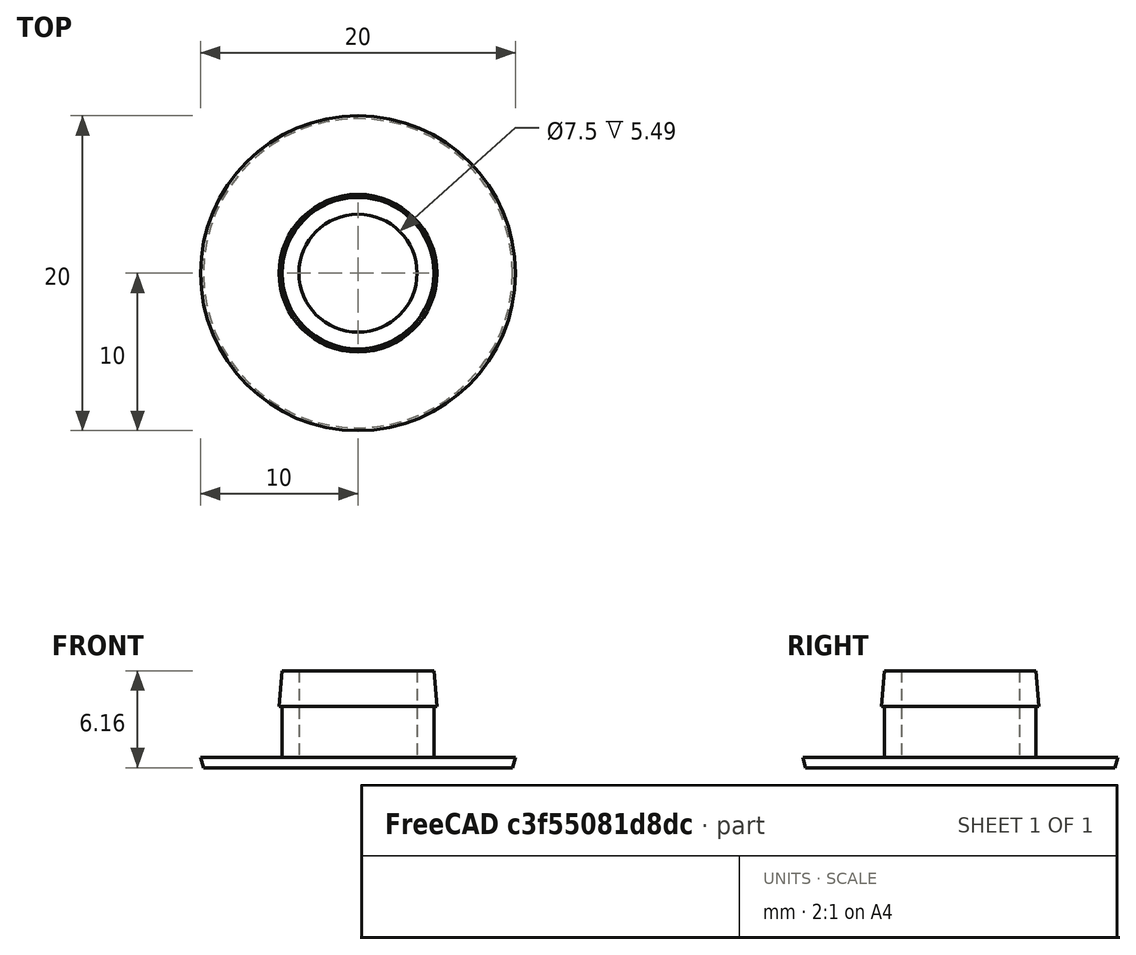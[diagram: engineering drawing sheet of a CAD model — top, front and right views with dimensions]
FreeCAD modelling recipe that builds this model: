
FCSTD DOCUMENT  (FreeCAD 0.20R29177 +426 (Git))
Label: door_threshold_screw_cover_9_3mm
License: Creative Commons Attribution
LicenseURL: http://creativecommons.org/licenses/by/3.0/
objects: Sketcher::SketchObject×1, PartDesign::Revolution×1, PartDesign::Body×1, Mesh::Feature×1
note: 4 computed .brp shape members not serialized (recipe doc carries the construction recipe); baked Part::Feature solids carry a one-line shape summary decoded from their .brp

FEATURE [Sketcher::SketchObject] Sketch
  FullyConstrained = true
  MapMode = 5
  Placement = pos=(0,0,0) rot=(1,0,0;1.5708rad)
  Support = -> [XZ_Plane]
  expr: .Constraints.Inner = 9.640000000000001 / 2
  expr: .Constraints.Outer = 20 / 2
  expr: Constraints[10] = .Constraints.Inner
  expr: Constraints[19] = .Constraints.Thickness
  expr: Constraints[20] = 7.5 / 2
  expr: Constraints[26] = .Constraints.Inner
  sketch-geometry (11):
    g0: LineSegment StartX=0 StartY=0 StartZ=0 EndX=-4.82 EndY=0 EndZ=0
    g1: LineSegment StartX=-10 StartY=0.67 StartZ=0 EndX=-4.82 EndY=0.67 EndZ=0
    g2: LineSegment StartX=-4.82 StartY=0.67 StartZ=0 EndX=-4.82 EndY=3.91 EndZ=0
    g3: LineSegment StartX=-4.82 StartY=3.91 StartZ=0 EndX=-5.01 EndY=3.91 EndZ=0
    g4: LineSegment StartX=-5.01 StartY=3.91 StartZ=0 EndX=-4.82 EndY=6.16 EndZ=0
    g5: LineSegment StartX=-4.82 StartY=6.16 StartZ=0 EndX=-3.75 EndY=6.16 EndZ=0
    g6: LineSegment StartX=-3.75 StartY=6.16 StartZ=0 EndX=-3.75 EndY=0.67 EndZ=0
    g7: LineSegment StartX=-3.75 StartY=0.67 StartZ=0 EndX=0 EndY=0.67 EndZ=0
    g8: LineSegment StartX=0 StartY=0.67 StartZ=0 EndX=0 EndY=0 EndZ=0
    g9: LineSegment StartX=-4.82 StartY=0 StartZ=0 EndX=-9.82 EndY=0 EndZ=0
    g10: LineSegment StartX=-9.82 StartY=0 StartZ=0 EndX=-10 EndY=0.67 EndZ=0
  constraints (32):
    c: Coincident(g-1,g0)
    c: PointOnObject(g0,g-1)
    c: Horizontal(g1)
    c: Coincident(g1,g2)
    c: Vertical(g2)
    c: Coincident(g2,g3)
    c: Horizontal(g3)
    c: Coincident(g3,g4)
    c: DistanceX(g1,g0) = 10  'Outer'
    c: DistanceX(g0,g0) = 4.82  'Inner'
    c: DistanceX(g1,g0) = 4.82
    c: DistanceY(g0,g1) = 0.67  'Thickness'
    c: Coincident(g4,g5)
    c: Horizontal(g5)
    c: Coincident(g5,g6)
    c: Vertical(g6)
    c: Coincident(g6,g7)
    c: Horizontal(g7)
    c: Coincident(g7,g8)
    c: DistanceY(g0,g7) = 0.67
    c: DistanceX(g6,g7) = 3.75
    c: DistanceX(g3,g5) = 1.26
    c: Vertical(g8)
    c: Coincident(g8,g0)
    c: DistanceY(g0,g5) = 6.16  'Depth'
    c: DistanceY(g0,g2) = 3.91
    c: DistanceX(g4,g7) = 4.82
    c: Horizontal(g9)
    c: Coincident(g9,g10)
    c: Coincident(g1,g10)
    c: Coincident(g9,g0)
    c: DistanceX(g9,g9) = 5
FEATURE [PartDesign::Revolution] Revolution
  Angle = 360
  Axis = (0,2e-16,1)
  Base = (0,0,0)
  Placement = pos=(0,0,0) rot=(1,0,0;1.5708rad)
  Profile = -> Sketch
  ReferenceAxis = -> Sketch [V_Axis]
FEATURE [PartDesign::Body] Body
  Group = -> [Sketch,Revolution]
  Origin = -> Origin
  Tip = -> Revolution
FEATURE [Mesh::Feature] Mesh  label="Revolution (Meshed)"
